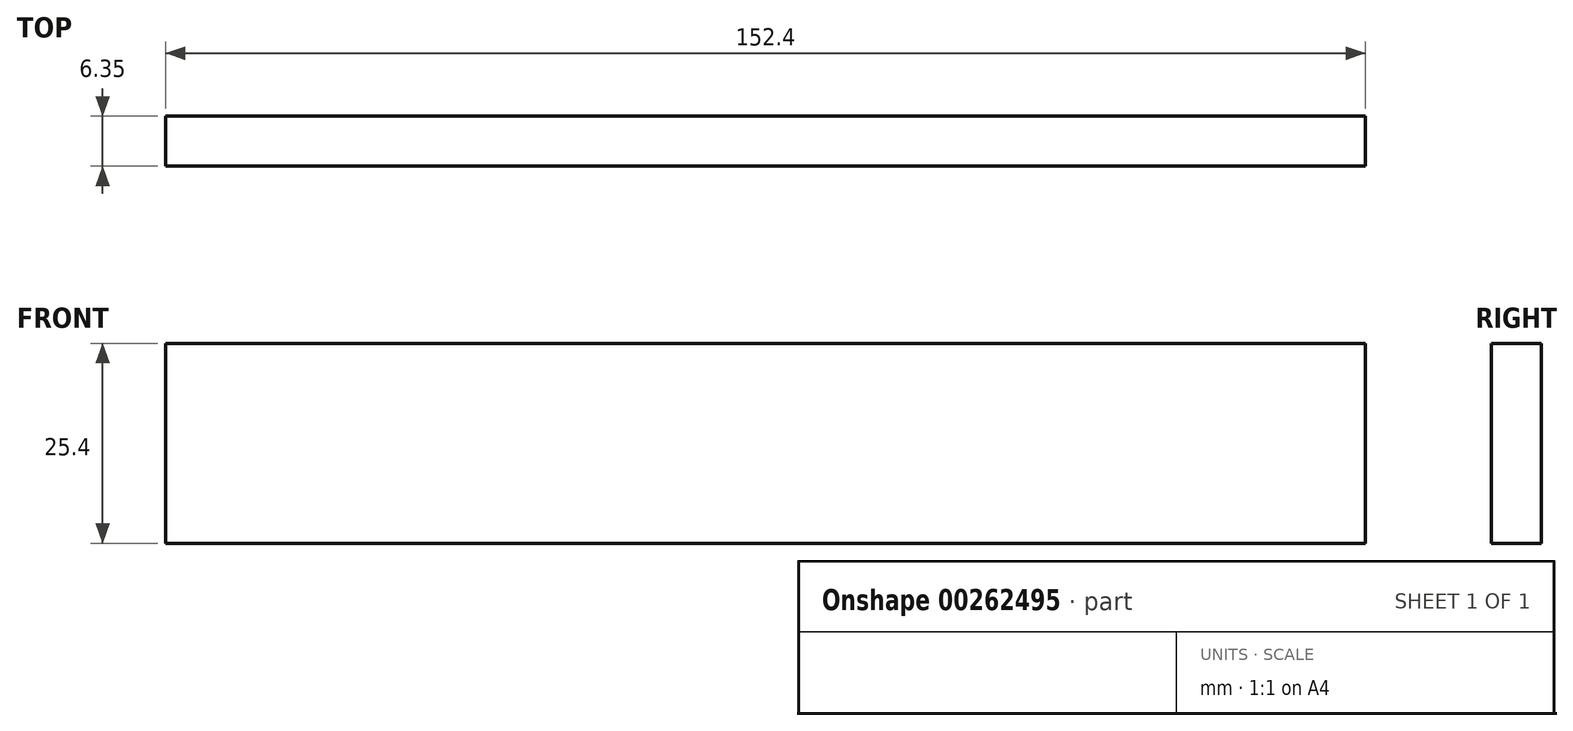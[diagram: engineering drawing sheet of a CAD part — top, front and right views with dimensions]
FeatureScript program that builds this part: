
annotation { "Feature Type Name" : "Feature", "Feature Type Description" : "" }
export const myFeature = defineFeature(function(context is Context, id is Id, definition is map)
    precondition{}
    {
        {
            var Q0;
            Q0=qCreatedBy(makeId("Front.planeOp"),FACE);
            var sketch = newSketch(context, id + "F0", { "sketchPlane" : qUnion([Q0])});
            skLineSegment(sketch, "E0.bottom", {"start": v(-152.4, -26.76) * mm, "end": v(0, -26.76) * mm});
            skLineSegment(sketch, "E0.top", {"start": v(-152.4, -52.16) * mm, "end": v(0, -52.16) * mm});
            skLineSegment(sketch, "E0.left", {"start": v(-152.4, -26.76) * mm, "end": v(-152.4, -52.16) * mm});
            skLineSegment(sketch, "E0.right", {"start": v(0, -26.76) * mm, "end": v(0, -52.16) * mm});
            skSolve(sketch);
        }
        {
            var Q0;
            Q0 = qSketchRegion(id + "F0", true);
            extrude(context, id + "F1", {"entities" : qUnion([Q0]), "depth" : 6.35 * mm});
        }
    });
